# Revit family: FR_PG-3000_simple
name_source: partatom
category: Allgemeines Modell
revit_build: Autodesk Revit 2018 (Build: 20181015_0930(x64)
units: mm (PartAtom-declared; Revit-internal decimal feet)

## family parameters
Beim Laden mit Abzugskörper schneiden = Ja
Bemaßung runder Anschluss = Durchmesser verwenden
Gemeinsam genutzt = Ja
Kann Basisbauteil für Bewehrung sein = Nein
OmniClass-Nummer = 23.70.50.00
OmniClass-Titel = Liquid Waste Handling Services
Raumberechnungspunkt = Nein
Teiletyp = Normal

## types (1)
- MEADrain PG 3000 vereinfacht
    Bauelement = Caniveau Surface de l'eau
    Beschreibung = Monolithische Entwässerungsrinnen aus Polymerbeton Bauhöhe 50 mm
    Construction, Élement de drainage = Kammrinne
    Documents de mise en œuvre = conformément aux dessins et à la description du produits
    Fiche technique produit = https://www.mea-group.com
    Hauteur = 50 mm  [stored 0.164042 ft]
    Hersteller = MEA Bautechnik GmbH business unite MEA Water Management
    IfcDescription = Monolithische Entwässerungsrinnen aus Polymerbeton Bauhöhe 50 mm
    IfcExportAs = IfcWasteTerminalType
    IfcExportType = USERDEFINED
    Largeur = 300 mm
    Largeur utile = 300 mm
    Largeur utile d'élément de drainage = 300
    MEA Planungshilfe = https://www.mea-group.com
    Materiaux = Polymerbeton
    Materiaux, enrobage / la fondation = PCC-Mörtel/Epoxy-Mörtel
    Poids = 22.8KGM
    Référence (Art. Nr.) = 010155694
    STLB-Bau Mustervorlage = https://www.stlb-bau-online.de
    Type Élement de drainage = Typ M
    URL = https://www.mea-group.com
    classe de charge caniveau = C 250
    guid = cf6c1bd8-9bf4-4563-8c57-07955e2378ac
    technique de montage = Caniveau seul
    élement de drainage = Canoveau de drainage

note: [stored X ft] marks values corroborated as IEEE doubles in the binary element streams (Revit-internal decimal feet)

## geometry (parser evidence)
native form markers: Extrusion x4
no freeform markers — native parametric forms only
